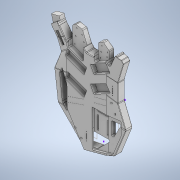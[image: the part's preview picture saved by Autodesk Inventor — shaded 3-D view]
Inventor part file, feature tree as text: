
AUTODESK INVENTOR PART (.ipt)
format: ipt  version: 2020 (Build 240168000, 168)  size: 2,281,984 bytes
history: native  units: mm
features: extrude x27, sketch x17, plane x11, other x11, sweep x4, fillet x3, projected_geometry x2
ambient origin geometry x8: Origin, YZ Plane, XZ Plane, XY Plane, X Axis, Y Axis, Z Axis, Center Point
bodies: Volumenkörper1 (feature_tree)
feature tree (75):
  extrude  "Extrusion1"  TaperAngle=0.0deg  [1 undecoded]
  sketch  "Skizze3"  dims[d4=20.0mm d5=0.0mm d6=35.0mm d7=0.0mm]
  extrude  "Extrusion2"  Depth=35.0mm TaperAngle=0.0deg
  extrude  "Extrusion3"  TaperAngle=0.0deg  [1 undecoded]
  extrude  "Extrusion4"  Depth=5.0mm TaperAngle=0.0deg
  sketch  "Skizze4"  dims[d8=2.5mm d9=0.0mm d12=0.0mm d13=0.0mm]
  extrude  "Extrusion5"  Depth=20.0mm TaperAngle=0.0deg
  extrude  "Extrusion7"  Depth=20.0mm TaperAngle=0.0deg
  extrude  "Extrusion9"  Depth=0.1mm
  extrude  "Extrusion10"  TaperAngle=0.0deg  [1 undecoded]
  extrude  "Extrusion11"  Depth=0.5mm
  extrude  "Extrusion17"  Depth=0.5mm
  sketch  "Skizze11"  dims[d20=32.0mm d21=0.0mm d32=20.0mm d33=0.0mm]
  extrude  "Extrusion18"  Depth=7.5mm
  extrude  "Extrusion19"  Depth=0.5mm
  plane  "Arbeitsebene1"
  sketch  "Skizze13"  dims[d34=3.0mm d35=0.0mm d36=20.0mm d37=0.0mm]
  plane  "Arbeitsebene4"
  other  "Trennen1"
  plane  "Arbeitsebene5"
  sketch  "Skizze18"  dims[d46=0.0mm d47=90.0deg d48=0.0mm d49=90.0deg]
  plane  "Arbeitsebene6"
  sketch  "Skizze19"  dims[d50=0.5mm d51=0.5mm]
  extrude  "Extrusion20"  Depth=0.5mm
  other  "Trennen3"
  plane  "Arbeitsebene8"
  sketch  "Skizze23"  dims[d54=9.0mm d55=7.5mm]
  sweep  "Sweeping1"
  sweep  "Sweeping4"
  plane  "Arbeitsebene9"
  sweep  "Sweeping5"
  plane  "Arbeitsebene10"
  sweep  "Sweeping6"
  fillet  "Rundung3"  Radius=3.0mm
  extrude  "Extrusion22"  Depth=2.3mm
  fillet  "Rundung4"  [1 undecoded]
  fillet  "Rundung5"  [1 undecoded]
  extrude  "Extrusion23"  Depth=6.0mm
  plane  "Arbeitsebene12"
  plane  "Arbeitsebene15"
  extrude  "Extrusion25"  TaperAngle=0.0deg  [1 undecoded]
  extrude  "Extrusion27"  Depth=6.0mm
  extrude  "Extrusion28"  TaperAngle=0.0deg  [1 undecoded]
  extrude  "Extrusion29"  Depth=3.0mm
  extrude  "Extrusion30"  Depth=3.0mm
  extrude  "Extrusion31"  Depth=2.574635mm
  extrude  "Extrusion33"  Depth=3.2mm
  plane  "Arbeitsebene16"
  sketch  "Skizze33"  dims[d76=0.0mm d77=90.0deg d82=6.0mm d83=3.0mm d84=2.3mm d85=0.0mm d86=0.0mm d91=0.0mm d92=0.0mm d93=6.0mm d94=3.0mm d95=2.3mm d96=0.0mm d97=0.0mm d98=6.0mm d99=3.0mm d100=2.3mm d101=0.0mm d102=0.0mm d103=3.0mm d104=3.0mm d105=3.0mm d106=3.0mm d107=3.0mm d108=3.0mm d121=2.574635mm d122=3.2mm d123=0.0mm d124=0.0mm d125=3.0mm d126=3.0mm d127=3.0mm d128=3.0mm d129=3.0mm d130=3.0mm d131=35.0mm d132=0.0mm d135=90.0deg d139=-0.541052mm d141=-14.3mm d142=17.551mm d143=0.0mm d144=15.0mm d145=0.0mm d146=33.0mm d147=0.0mm d148=36.0mm d149=0.0mm d150=42.0mm d151=0.0mm d152=40.0mm d153=0.0mm d154=40.0mm d155=0.0mm d156=26.0mm d157=0.0mm d158=25.0mm d159=0.0mm d160=47.25mm d161=10.0mm d162=0.0mm d163=10.0mm d164=0.0mm d167=4.0mm d168=0.0mm d169=0.0mm]
  extrude  "Extrusion34"  TaperAngle=0.0deg  [1 undecoded]
  extrude  "Extrusion35"  Depth=3.0mm
  extrude  "Extrusion26"  Depth=3.0mm
  extrude  "Extrusion32"  Depth=3.0mm
  extrude  "Extrusion36"  Depth=3.0mm
  sketch  "Skizze2"  dims[d0=45.0mm d1=0.0mm d2=0.0mm d3=0.0mm]
  sketch  "Skizze10"  dims[d16=13.0mm d17=0.0mm d18=5.0mm d19=0.0mm]
  sketch  "Skizze16"  dims[d38=-10.0mm d45=0.1mm]
  other  "Flä2"
  projected_geometry  "Projizierte Kontur1"
  sketch  "Skizze20"  dims[d52=0.5mm d53=0.5mm]
  other  "Flä4"
  other  "3D-Skizze1"
  other  "3D-Skizze4"
  other  "3D-Skizze5"
  other  "3D-Skizze6"
  sketch  "Skizze27"  dims[d60=3.5mm d61=0.5mm]
  projected_geometry  "Projizierte Kontur2"
  other  "Arbeitsachse3"
  plane  "Arbeitsebene13"
  sketch  "Skizze29"  dims[d62=0.5mm d67=6.35mm]
  sketch  "Skizze30"  dims[d68=3.0mm d69=0.0mm d74=0.0mm d75=90.0deg]
  other  "Erhabene Fläche2"
  other  "Erhabene Fläche4"
  sketch  "Skizze24"  dims[d56=-10.0mm d57=0.5mm]
  sketch  "Skizze25"  dims[d58=0.5mm d59=0.5mm]
note: 8 required parameter values undecoded (feature->parameter linkage not recoverable at this tier; creation-order binding heuristic only, values carry confidence <= 0.55)
